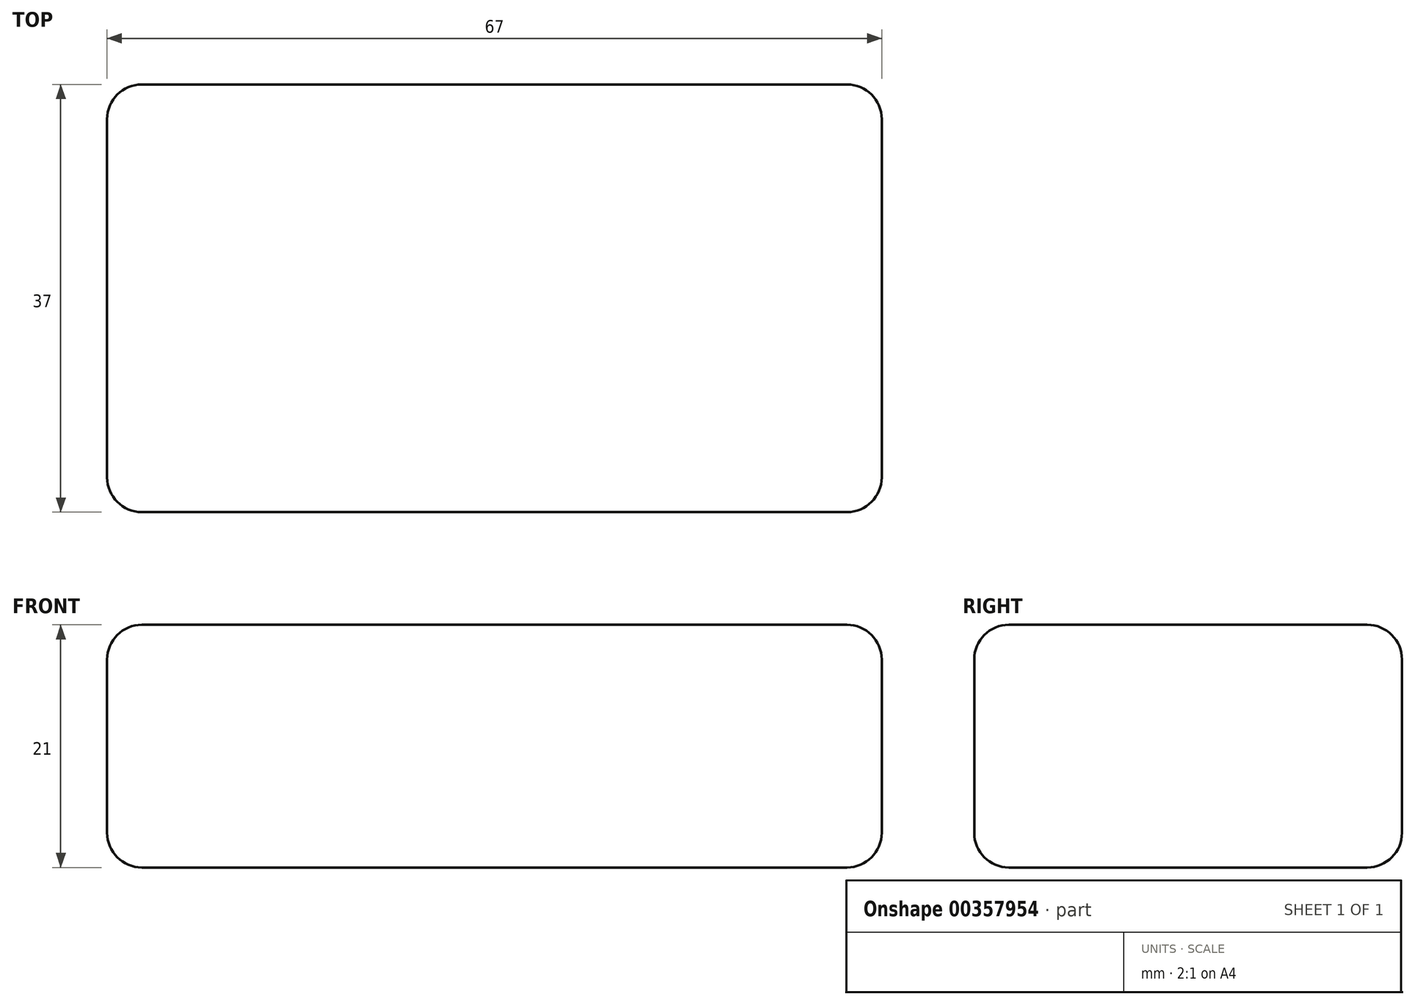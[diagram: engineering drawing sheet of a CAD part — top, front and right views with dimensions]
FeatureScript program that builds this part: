
annotation { "Feature Type Name" : "Feature", "Feature Type Description" : "" }
export const myFeature = defineFeature(function(context is Context, id is Id, definition is map)
    precondition{}
    {
        {
            var Q0;
            Q0=qCreatedBy(makeId("Top.planeOp"),FACE);
            var sketch = newSketch(context, id + "F0", { "sketchPlane" : qUnion([Q0])});
            skLineSegment(sketch, "E0.bottom", {"start": v(-33.5, 18.5) * mm, "end": v(33.5, 18.5) * mm});
            skLineSegment(sketch, "E0.top", {"start": v(-33.5, -18.5) * mm, "end": v(33.5, -18.5) * mm});
            skLineSegment(sketch, "E0.left", {"start": v(-33.5, 18.5) * mm, "end": v(-33.5, -18.5) * mm});
            skLineSegment(sketch, "E0.right", {"start": v(33.5, 18.5) * mm, "end": v(33.5, -18.5) * mm});
            skSolve(sketch);
        }
        {
            var Q0;
            Q0 = qSketchRegion(id + "F0", true);
            extrude(context, id + "F1", {"entities" : qUnion([Q0]), "depth" : 21 * mm});
        }
        {
            var Q0;
            Q0=makeQuery(id+"F1.opExtrude","CAP_EDGE",EDGE,{"disambiguationData":[OSD([sQuery(id+"F0.wireOp",EDGE,"E0.top")])],"isStart":false});
            var Q1;
            Q1=makeQuery(id+"F1.opExtrude","SWEPT_EDGE",EDGE,{"disambiguationData":[OSD([sQuery(id+"F0.wireOp",EDGE,"E0.bottom"),sQuery(id+"F0.wireOp",EDGE,"E0.right")])]});
            var Q2;
            Q2=makeQuery(id+"F1.opExtrude","SWEPT_EDGE",EDGE,{"disambiguationData":[OSD([sQuery(id+"F0.wireOp",EDGE,"E0.top"),sQuery(id+"F0.wireOp",EDGE,"E0.left")])]});
            var Q3;
            Q3=makeQuery(id+"F1.opExtrude","SWEPT_EDGE",EDGE,{"disambiguationData":[OSD([sQuery(id+"F0.wireOp",EDGE,"E0.top"),sQuery(id+"F0.wireOp",EDGE,"E0.right")])]});
            var Q4;
            Q4=makeQuery(id+"F1.opExtrude","CAP_EDGE",EDGE,{"disambiguationData":[OSD([sQuery(id+"F0.wireOp",EDGE,"E0.bottom")])],"isStart":false});
            var Q5;
            Q5=makeQuery(id+"F1.opExtrude","CAP_EDGE",EDGE,{"disambiguationData":[OSD([sQuery(id+"F0.wireOp",EDGE,"E0.top")])],"isStart":true});
            var Q6;
            Q6=makeQuery(id+"F1.opExtrude","CAP_EDGE",EDGE,{"disambiguationData":[OSD([sQuery(id+"F0.wireOp",EDGE,"E0.left")])],"isStart":false});
            var Q7;
            Q7=makeQuery(id+"F1.opExtrude","CAP_EDGE",EDGE,{"disambiguationData":[OSD([sQuery(id+"F0.wireOp",EDGE,"E0.right")])],"isStart":true});
            var Q8;
            Q8=makeQuery(id+"F1.opExtrude","CAP_EDGE",EDGE,{"disambiguationData":[OSD([sQuery(id+"F0.wireOp",EDGE,"E0.right")])],"isStart":false});
            var Q9;
            Q9=makeQuery(id+"F1.opExtrude","SWEPT_EDGE",EDGE,{"disambiguationData":[OSD([sQuery(id+"F0.wireOp",EDGE,"E0.bottom"),sQuery(id+"F0.wireOp",EDGE,"E0.left")])]});
            var Q10;
            Q10=makeQuery(id+"F1.opExtrude","CAP_EDGE",EDGE,{"disambiguationData":[OSD([sQuery(id+"F0.wireOp",EDGE,"E0.bottom")])],"isStart":true});
            var Q11;
            Q11=makeQuery(id+"F1.opExtrude","CAP_EDGE",EDGE,{"disambiguationData":[OSD([sQuery(id+"F0.wireOp",EDGE,"E0.left")])],"isStart":true});
            fillet(context, id + "F2", {"entities" : qUnion([Q0, Q1, Q2, Q3, Q4, Q5, Q6, Q7, Q8, Q9, Q10, Q11]), "radius" : 3 * mm, "tangentPropagation" : true, "allowEdgeOverflow" : false});
        }
    });
